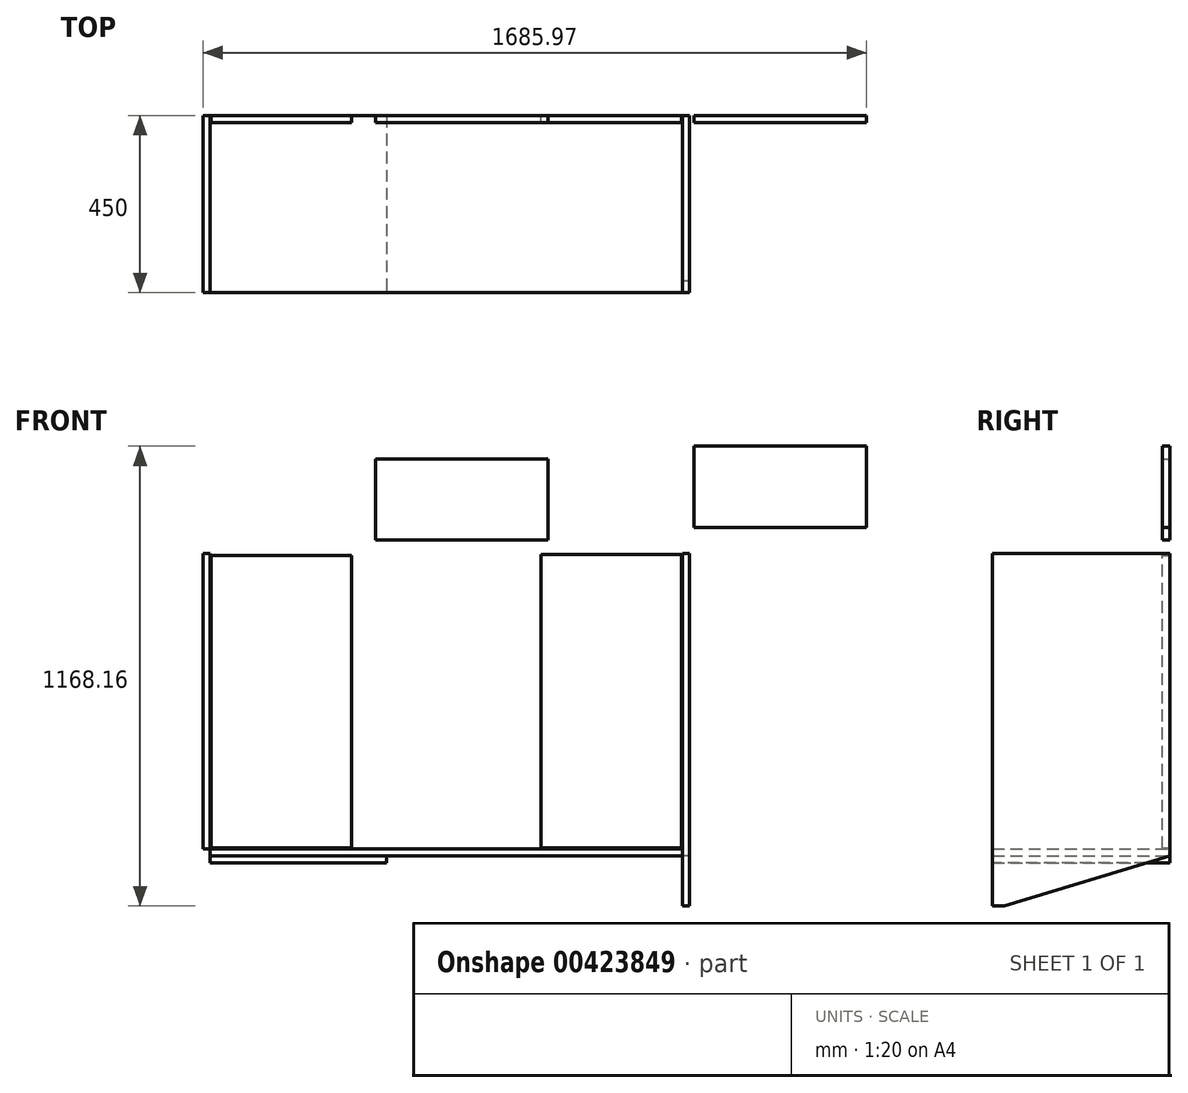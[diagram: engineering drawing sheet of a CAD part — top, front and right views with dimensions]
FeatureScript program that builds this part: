
annotation { "Feature Type Name" : "Feature", "Feature Type Description" : "" }
export const myFeature = defineFeature(function(context is Context, id is Id, definition is map)
    precondition{}
    {
        {
            var Q0;
            Q0=qCreatedBy(makeId("Top.planeOp"),FACE);
            var sketch = newSketch(context, id + "F0", { "sketchPlane" : qUnion([Q0])});
            skLineSegment(sketch, "E0.bottom", {"start": v(600, -225) * mm, "end": v(-600, -225) * mm});
            skLineSegment(sketch, "E0.top", {"start": v(600, 225) * mm, "end": v(-600, 225) * mm});
            skLineSegment(sketch, "E0.left", {"start": v(600, -225) * mm, "end": v(600, 225) * mm});
            skLineSegment(sketch, "E0.right", {"start": v(-600, -225) * mm, "end": v(-600, 225) * mm});
            skPoint(sketch, "E0.middle", {"position": v(0, 0) * mm});
            skSolve(sketch);
        }
        {
            var Q0;
            Q0=qSketchRegion(id+"F0",true);
            extrude(context, id + "F1", {"entities" : qUnion([Q0]), "depth" : 18 * mm});
        }
        {
            var Q0;
            Q0=makeQuery(id+"F1.opExtrude","SWEPT_FACE",FACE,{"disambiguationData":[OSD([sQuery(id+"F0.wireOp",EDGE,"E0.top")])]});
            var sketch = newSketch(context, id + "F2", { "sketchPlane" : qUnion([Q0])});
            skLineSegment(sketch, "E1.bottom", {"start": v(-598, 20) * mm, "end": v(-241, 20) * mm});
            skLineSegment(sketch, "E1.top", {"start": v(-598, 766) * mm, "end": v(-241, 766) * mm});
            skLineSegment(sketch, "E1.left", {"start": v(-598, 20) * mm, "end": v(-598, 766) * mm});
            skLineSegment(sketch, "E1.right", {"start": v(-241, 20) * mm, "end": v(-241, 766) * mm});
            skLineSegment(sketch, "E2.bottom", {"start": v(598, 20) * mm, "end": v(241, 20) * mm});
            skLineSegment(sketch, "E2.top", {"start": v(598, 764) * mm, "end": v(241, 764) * mm});
            skLineSegment(sketch, "E2.left", {"start": v(598, 20) * mm, "end": v(598, 764) * mm});
            skLineSegment(sketch, "E2.right", {"start": v(241, 18) * mm, "end": v(241, 764) * mm});
            skLineSegment(sketch, "E3.bottom", {"start": v(-1067.97, 1041.16) * mm, "end": v(-629.97, 1041.16) * mm});
            skLineSegment(sketch, "E3.top", {"start": v(-1067.97, 835.16) * mm, "end": v(-629.97, 835.16) * mm});
            skLineSegment(sketch, "E3.left", {"start": v(-1067.97, 1041.16) * mm, "end": v(-1067.97, 835.16) * mm});
            skLineSegment(sketch, "E3.right", {"start": v(-629.97, 1041.16) * mm, "end": v(-629.97, 835.16) * mm});
            skLineSegment(sketch, "E4.bottom", {"start": v(-258.08, 1008.52) * mm, "end": v(179.92, 1008.52) * mm});
            skLineSegment(sketch, "E4.top", {"start": v(-258.08, 802.52) * mm, "end": v(179.92, 802.52) * mm});
            skLineSegment(sketch, "E4.left", {"start": v(-258.08, 1008.52) * mm, "end": v(-258.08, 802.52) * mm});
            skLineSegment(sketch, "E4.right", {"start": v(179.92, 1008.52) * mm, "end": v(179.92, 802.52) * mm});
            skSolve(sketch);
        }
        {
            var Q0;
            Q0=qSketchRegion(id+"F2",true);
            extrude(context, id + "F3", {"entities" : qUnion([Q0]), "oppositeDirection" : true, "depth" : 18 * mm});
        }
        {
            var Q0;
            Q0=makeQuery(id+"F1.opExtrude","SWEPT_FACE",FACE,{"disambiguationData":[OSD([sQuery(id+"F0.wireOp",EDGE,"E0.left")])]});
            var sketch = newSketch(context, id + "F4", { "sketchPlane" : qUnion([Q0])});
            skLineSegment(sketch, "E5", {"start": v(-225, -127) * mm, "end": v(-195, -127) * mm});
            skLineSegment(sketch, "E6", {"start": v(225, 0) * mm, "end": v(225, 768) * mm});
            skLineSegment(sketch, "E7", {"start": v(225, 768) * mm, "end": v(-225, 768) * mm});
            skLineSegment(sketch, "E8", {"start": v(-225, 768) * mm, "end": v(-225, -127) * mm});
            skLineSegment(sketch, "E9", {"start": v(-195, -127) * mm, "end": v(225, 0) * mm});
            skSolve(sketch);
        }
        {
            var Q0;
            Q0=qSketchRegion(id+"F4",true);
            extrude(context, id + "F5", {"entities" : qUnion([Q0]), "depth" : 18 * mm});
        }
        {
            var Q0;
            Q0=makeQuery(id+"F1.opExtrude","SWEPT_FACE",FACE,{"disambiguationData":[OSD([sQuery(id+"F0.wireOp",EDGE,"E0.right")])]});
            var sketch = newSketch(context, id + "F6", { "sketchPlane" : qUnion([Q0])});
            skLineSegment(sketch, "E10.bottom", {"start": v(-225, 18) * mm, "end": v(225, 18) * mm});
            skLineSegment(sketch, "E10.top", {"start": v(-225, 768) * mm, "end": v(225, 768) * mm});
            skLineSegment(sketch, "E10.left", {"start": v(-225, 18) * mm, "end": v(-225, 768) * mm});
            skLineSegment(sketch, "E10.right", {"start": v(225, 18) * mm, "end": v(225, 768) * mm});
            skSolve(sketch);
        }
        {
            var Q0;
            Q0=qSketchRegion(id+"F6",true);
            extrude(context, id + "F7", {"entities" : qUnion([Q0]), "depth" : 18 * mm});
        }
        {
            var Q0;
            Q0=makeQuery(id+"F1.opExtrude","CAP_FACE",FACE,{"disambiguationData":[OSD([sQuery(id+"F0.wireOp",EDGE,"E0.bottom"),sQuery(id+"F0.wireOp",EDGE,"E0.top"),sQuery(id+"F0.wireOp",EDGE,"E0.left"),sQuery(id+"F0.wireOp",EDGE,"E0.right")])],"isStart":true});
            var sketch = newSketch(context, id + "F8", { "sketchPlane" : qUnion([Q0])});
            skLineSegment(sketch, "E11.bottom", {"start": v(-600, -225) * mm, "end": v(-152, -225) * mm});
            skLineSegment(sketch, "E11.top", {"start": v(-600, 225) * mm, "end": v(-152, 225) * mm});
            skLineSegment(sketch, "E11.left", {"start": v(-600, -225) * mm, "end": v(-600, 225) * mm});
            skLineSegment(sketch, "E11.right", {"start": v(-152, -225) * mm, "end": v(-152, 225) * mm});
            skSolve(sketch);
        }
        {
            var Q0;
            Q0=qSketchRegion(id+"F8",true);
            extrude(context, id + "F9", {"entities" : qUnion([Q0]), "depth" : 18 * mm});
        }
    });
